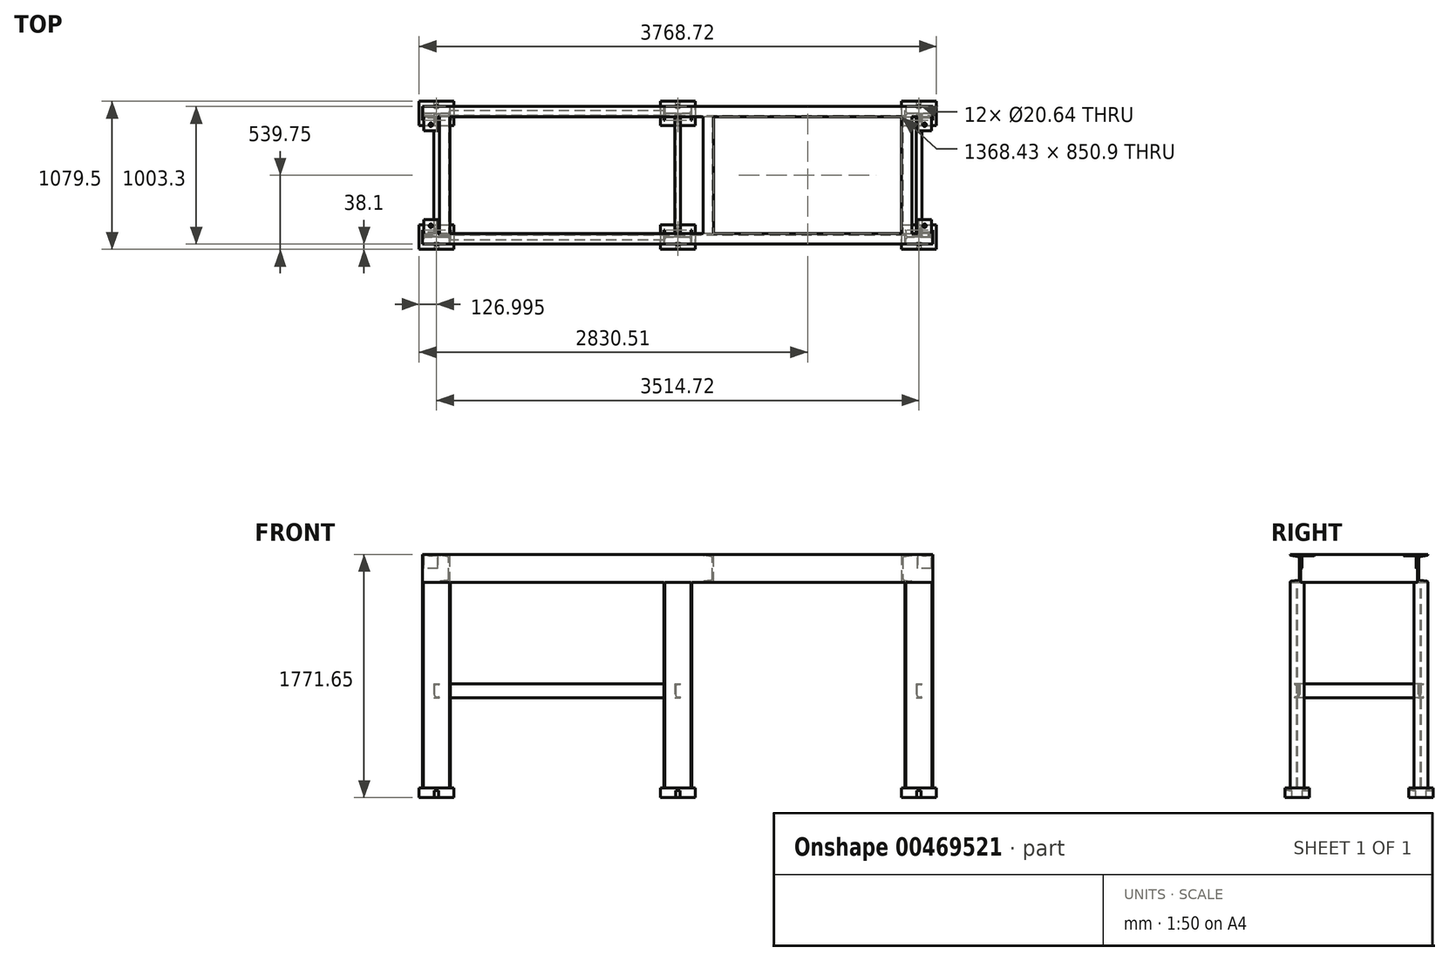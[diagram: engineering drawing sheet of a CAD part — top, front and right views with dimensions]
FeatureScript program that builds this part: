
annotation { "Feature Type Name" : "Feature", "Feature Type Description" : "" }
export const myFeature = defineFeature(function(context is Context, id is Id, definition is map)
    precondition{}
    {
        {
            var Q0;
            Q0=qCreatedBy(makeId("Right.planeOp"),FACE);
            var sketch = newSketch(context, id + "F0", { "sketchPlane" : qUnion([Q0])});
            skLineSegment(sketch, "E0", {"start": v(0, 0) * mm, "end": v(0, -101.6) * mm});
            skLineSegment(sketch, "E1", {"start": v(0, 0) * mm, "end": v(101.6, 0) * mm});
            skLineSegment(sketch, "E2", {"start": v(101.6, 0) * mm, "end": v(101.6, -4.76) * mm});
            skLineSegment(sketch, "E3", {"start": v(0, -101.6) * mm, "end": v(4.76, -101.6) * mm});
            skArc(sketch, "E4", {"start": v(4.76, -101.6) * mm, "mid": v(8.13, -100.2) * mm, "end": v(9.53, -96.84) * mm});
            skArc(sketch, "E5", {"start": v(96.84, -9.53) * mm, "mid": v(100.2, -8.13) * mm, "end": v(101.6, -4.76) * mm});
            skArc(sketch, "E6", {"start": v(19.05, -9.53) * mm, "mid": v(12.31, -12.31) * mm, "end": v(9.52, -19.05) * mm});
            skLineSegment(sketch, "E7", {"start": v(9.53, -96.84) * mm, "end": v(9.53, -19.05) * mm});
            skLineSegment(sketch, "E8", {"start": v(96.84, -9.53) * mm, "end": v(19.05, -9.53) * mm});
            skSolve(sketch);
        }
        {
            var Q0;
            Q0 = qSketchRegion(id + "F0", true);
            extrude(context, id + "F1", {"entities" : qUnion([Q0]), "endBound" : BoundingType.SYMMETRIC, "depth" : 101.6 * mm, "offsetDistance" : 25.4 * mm});
        }
        {
            var Q0;
            Q0=qCreatedBy(makeId("Right.planeOp"),FACE);
            var sketch = newSketch(context, id + "F2", { "sketchPlane" : qUnion([Q0])});
            skLineSegment(sketch, "E9", {"start": v(0, 0) * mm, "end": v(0, -203.2) * mm});
            skLineSegment(sketch, "E10", {"start": v(0, -203.2) * mm, "end": v(-76.2, -203.2) * mm});
            skLineSegment(sketch, "E11", {"start": v(0, 0) * mm, "end": v(-76.2, 0) * mm});
            skLineSegment(sketch, "E12", {"start": v(-9.53, -28.58) * mm, "end": v(-9.52, -174.62) * mm});
            skLineSegment(sketch, "E13", {"start": v(-19.35, -186.32) * mm, "end": v(-69.4, -195.1) * mm});
            skLineSegment(sketch, "E14", {"start": v(-19.35, -16.88) * mm, "end": v(-69.4, -8.1) * mm});
            skArc(sketch, "E15", {"start": v(-69.4, -195.1) * mm, "mid": v(-74.27, -197.91) * mm, "end": v(-76.2, -203.2) * mm});
            skArc(sketch, "E16", {"start": v(-76.2, 0) * mm, "mid": v(-74.27, -5.29) * mm, "end": v(-69.4, -8.1) * mm});
            skArc(sketch, "E17", {"start": v(-9.53, -28.58) * mm, "mid": v(-12.3, -20.94) * mm, "end": v(-19.35, -16.88) * mm});
            skArc(sketch, "E18", {"start": v(-19.35, -186.32) * mm, "mid": v(-12.3, -182.26) * mm, "end": v(-9.52, -174.62) * mm});
            skSolve(sketch);
        }
        {
            var Q0;
            Q0 = qSketchRegion(id + "F2", true);
            extrude(context, id + "F3", {"entities" : qUnion([Q0]), "operationType" : NewBodyOperationType.ADD, "oppositeDirection" : true, "depth" : 60.32 * mm, "offsetDistance" : 25.4 * mm, "hasSecondDirection" : true, "secondDirectionOppositeDirection" : false, "secondDirectionDepth" : 3657.6 * mm});
        }
        {
            var Q0;
            Q0=qCreatedBy(makeId("Right.planeOp"),FACE);
            cPlane(context, id + "F4", {"entities" : qUnion([Q0]), "cplaneType" : CPlaneType.OFFSET, "offset" : 3597.27 * mm, "width" : 152.4 * mm, "height" : 152.4 * mm});
        }
        {
            var Q0;
            Q0=qCreatedBy(id+"F4.planeOp",FACE);
            var sketch = newSketch(context, id + "F5", { "sketchPlane" : qUnion([Q0])});
            skLineSegment(sketch, "E19", {"start": v(0, 0) * mm, "end": v(0, -101.6) * mm});
            skLineSegment(sketch, "E20", {"start": v(0, 0) * mm, "end": v(101.6, 0) * mm});
            skLineSegment(sketch, "E21", {"start": v(101.6, 0) * mm, "end": v(101.6, -4.76) * mm});
            skLineSegment(sketch, "E22", {"start": v(0, -101.6) * mm, "end": v(4.76, -101.6) * mm});
            skArc(sketch, "E23", {"start": v(4.76, -101.6) * mm, "mid": v(8.13, -100.2) * mm, "end": v(9.53, -96.84) * mm});
            skArc(sketch, "E24", {"start": v(96.84, -9.53) * mm, "mid": v(100.2, -8.13) * mm, "end": v(101.6, -4.76) * mm});
            skArc(sketch, "E25", {"start": v(19.05, -9.53) * mm, "mid": v(12.31, -12.31) * mm, "end": v(9.52, -19.05) * mm});
            skLineSegment(sketch, "E26", {"start": v(9.53, -96.84) * mm, "end": v(9.53, -19.05) * mm});
            skLineSegment(sketch, "E27", {"start": v(96.84, -9.53) * mm, "end": v(19.05, -9.53) * mm});
            skSolve(sketch);
        }
        {
            var Q0;
            Q0 = qSketchRegion(id + "F5", true);
            extrude(context, id + "F6", {"entities" : qUnion([Q0]), "operationType" : NewBodyOperationType.ADD, "endBound" : BoundingType.SYMMETRIC, "depth" : 101.6 * mm, "offsetDistance" : 25.4 * mm});
        }
        {
            var Q0;
            Q0=makeQuery(id+"F1.opExtrude","SWEPT_FACE",FACE,{"disambiguationData":[OSD([sQuery(id+"F0.wireOp",EDGE,"E1")])]});
            var sketch = newSketch(context, id + "F7", { "sketchPlane" : qUnion([Q0])});
            skCircle(sketch, "E28", {"center": v(0, 57.15) * mm, "radius": 12.7 * mm});
            skCircle(sketch, "E29", {"center": v(3597.28, 57.15) * mm, "radius": 12.7 * mm});
            skSolve(sketch);
        }
        {
            var Q0;
            Q0 = qSketchRegion(id + "F7", true);
            extrude(context, id + "F8", {"entities" : qUnion([Q0]), "operationType" : NewBodyOperationType.REMOVE, "endBound" : BoundingType.UP_TO_NEXT, "oppositeDirection" : true, "depth" : 25.4 * mm, "offsetDistance" : 25.4 * mm});
        }
        {
            var Q0;
            Q0=qCreatedBy(makeId("Front.planeOp"),FACE);
            cPlane(context, id + "F9", {"entities" : qUnion([Q0]), "cplaneType" : CPlaneType.OFFSET, "offset" : 425.45 * mm, "oppositeDirection" : true, "width" : 152.4 * mm, "height" : 152.4 * mm});
        }
        {
            var Q0;
            Q0=makeQuery(id+"F1.opExtrude","SWEPT_BODY",BODY,{"disambiguationData":[OSD([sQuery(id+"F0.wireOp",EDGE,"E0"),sQuery(id+"F0.wireOp",EDGE,"E1"),sQuery(id+"F0.wireOp",EDGE,"E2"),sQuery(id+"F0.wireOp",EDGE,"E3"),sQuery(id+"F0.wireOp",EDGE,"E4"),sQuery(id+"F0.wireOp",EDGE,"E5"),sQuery(id+"F0.wireOp",EDGE,"E6"),sQuery(id+"F0.wireOp",EDGE,"E7"),sQuery(id+"F0.wireOp",EDGE,"E8")])]});
            var Q1;
            Q1=qCreatedBy(id+"F9.planeOp",FACE);
            mirror(context, id + "F10", {"entities" : qUnion([Q0]), "mirrorPlane" : qUnion([Q1])});
        }
        {
            var Q0;
            Q0=makeQuery(id+"F3.opExtrude","SWEPT_FACE",FACE,{"disambiguationData":[OSD([sQuery(id+"F2.wireOp",EDGE,"E9")])]});
            var sketch = newSketch(context, id + "F11", { "sketchPlane" : qUnion([Q0])});
            skLineSegment(sketch, "E30", {"start": v(-3429, 0) * mm, "end": v(-3429, -203.2) * mm});
            skLineSegment(sketch, "E31", {"start": v(-3429, -203.2) * mm, "end": v(-3505.2, -203.2) * mm});
            skLineSegment(sketch, "E32", {"start": v(-3429, 0) * mm, "end": v(-3505.2, 0) * mm});
            skLineSegment(sketch, "E33", {"start": v(-3438.53, -28.58) * mm, "end": v(-3438.53, -174.62) * mm});
            skLineSegment(sketch, "E34", {"start": v(-3448.35, -186.32) * mm, "end": v(-3498.4, -195.1) * mm});
            skLineSegment(sketch, "E35", {"start": v(-3448.35, -16.88) * mm, "end": v(-3498.4, -8.1) * mm});
            skArc(sketch, "E36", {"start": v(-3498.4, -195.1) * mm, "mid": v(-3503.27, -197.91) * mm, "end": v(-3505.2, -203.2) * mm});
            skArc(sketch, "E37", {"start": v(-3505.2, 0) * mm, "mid": v(-3503.27, -5.29) * mm, "end": v(-3498.4, -8.1) * mm});
            skArc(sketch, "E38", {"start": v(-3438.52, -28.58) * mm, "mid": v(-3441.3, -20.94) * mm, "end": v(-3448.35, -16.88) * mm});
            skArc(sketch, "E39", {"start": v(-3448.35, -186.32) * mm, "mid": v(-3441.3, -182.26) * mm, "end": v(-3438.53, -174.62) * mm});
            skLineSegment(sketch, "E40", {"start": v(-2060.57, -203.2) * mm, "end": v(-2060.57, 0) * mm});
            skLineSegment(sketch, "E41", {"start": v(-2060.57, 0) * mm, "end": v(-1984.38, 0) * mm});
            skLineSegment(sketch, "E42", {"start": v(-2060.57, -203.2) * mm, "end": v(-1984.38, -203.2) * mm});
            skLineSegment(sketch, "E43", {"start": v(-2051.05, -174.62) * mm, "end": v(-2051.05, -28.58) * mm});
            skLineSegment(sketch, "E44", {"start": v(-2041.23, -16.88) * mm, "end": v(-1991.18, -8.1) * mm});
            skLineSegment(sketch, "E45", {"start": v(-2041.23, -186.32) * mm, "end": v(-1991.18, -195.1) * mm});
            skArc(sketch, "E46", {"start": v(-1991.18, -8.1) * mm, "mid": v(-1986.3, -5.29) * mm, "end": v(-1984.38, 0) * mm});
            skArc(sketch, "E47", {"start": v(-1984.38, -203.2) * mm, "mid": v(-1986.3, -197.91) * mm, "end": v(-1991.18, -195.1) * mm});
            skArc(sketch, "E48", {"start": v(-2051.05, -174.62) * mm, "mid": v(-2048.27, -182.26) * mm, "end": v(-2041.23, -186.32) * mm});
            skArc(sketch, "E49", {"start": v(-2041.23, -16.88) * mm, "mid": v(-2048.27, -20.94) * mm, "end": v(-2051.05, -28.58) * mm});
            skLineSegment(sketch, "E50", {"start": v(-139.7, -203.2) * mm, "end": v(-139.7, 0) * mm});
            skLineSegment(sketch, "E51", {"start": v(-139.7, 0) * mm, "end": v(-63.5, 0) * mm});
            skLineSegment(sketch, "E52", {"start": v(-139.7, -203.2) * mm, "end": v(-63.5, -203.2) * mm});
            skLineSegment(sketch, "E53", {"start": v(-130.17, -174.62) * mm, "end": v(-130.17, -28.58) * mm});
            skLineSegment(sketch, "E54", {"start": v(-120.35, -16.88) * mm, "end": v(-70.3, -8.1) * mm});
            skLineSegment(sketch, "E55", {"start": v(-120.35, -186.32) * mm, "end": v(-70.3, -195.1) * mm});
            skArc(sketch, "E56", {"start": v(-70.3, -8.1) * mm, "mid": v(-65.43, -5.29) * mm, "end": v(-63.5, 0) * mm});
            skArc(sketch, "E57", {"start": v(-63.5, -203.2) * mm, "mid": v(-65.43, -197.91) * mm, "end": v(-70.3, -195.1) * mm});
            skArc(sketch, "E58", {"start": v(-130.18, -174.62) * mm, "mid": v(-127.4, -182.26) * mm, "end": v(-120.35, -186.32) * mm});
            skArc(sketch, "E59", {"start": v(-120.35, -16.88) * mm, "mid": v(-127.4, -20.94) * mm, "end": v(-130.18, -28.58) * mm});
            skSolve(sketch);
        }
        {
            var Q0;
            Q0 = qSketchRegion(id + "F11", true);
            extrude(context, id + "F12", {"entities" : qUnion([Q0]), "operationType" : NewBodyOperationType.ADD, "endBound" : BoundingType.UP_TO_NEXT, "depth" : 25.4 * mm, "offsetDistance" : 25.4 * mm});
        }
        {
            var Q0;
            {var subQ0=makeQuery(id+"F3.opExtrude","SWEPT_FACE",FACE,{"disambiguationData":[OSD([sQuery(id+"F2.wireOp",EDGE,"E10")])]});Q0=makeQuery(id+"F12.boolean.opBoolean","MERGE",FACE,{"derivedFrom":[subQ0,makeQuery(id+"F10.opPattern","COPY",FACE,{"derivedFrom":subQ0,"instanceName":"1"}),makeQuery(id+"F12.opExtrude","SWEPT_FACE",FACE,{"disambiguationData":[OSD([sQuery(id+"F11.wireOp",EDGE,"E31")])]}),makeQuery(id+"F12.opExtrude","SWEPT_FACE",FACE,{"disambiguationData":[OSD([sQuery(id+"F11.wireOp",EDGE,"E42")])]}),makeQuery(id+"F12.opExtrude","SWEPT_FACE",FACE,{"disambiguationData":[OSD([sQuery(id+"F11.wireOp",EDGE,"E52")])]})]});}
            var sketch = newSketch(context, id + "F13", { "sketchPlane" : qUnion([Q0])});
            skLineSegment(sketch, "E60", {"start": v(-60.33, -825.5) * mm, "end": v(-60.33, -927.1) * mm});
            skLineSegment(sketch, "E61", {"start": v(-60.33, -927.1) * mm, "end": v(-53.98, -927.1) * mm});
            skLineSegment(sketch, "E62", {"start": v(-60.33, -825.5) * mm, "end": v(-53.98, -825.5) * mm});
            skLineSegment(sketch, "E63", {"start": v(142.87, -825.5) * mm, "end": v(142.87, -927.1) * mm});
            skLineSegment(sketch, "E64", {"start": v(142.87, -927.1) * mm, "end": v(136.53, -927.1) * mm});
            skLineSegment(sketch, "E65", {"start": v(142.87, -825.5) * mm, "end": v(136.52, -825.5) * mm});
            skLineSegment(sketch, "E66", {"start": v(-53.98, -825.5) * mm, "end": v(-53.98, -860.42) * mm});
            skLineSegment(sketch, "E67", {"start": v(-53.98, -927.1) * mm, "end": v(-53.98, -892.17) * mm});
            skLineSegment(sketch, "E68", {"start": v(136.52, -927.1) * mm, "end": v(136.52, -892.17) * mm});
            skLineSegment(sketch, "E69", {"start": v(136.52, -825.5) * mm, "end": v(136.52, -860.43) * mm});
            skLineSegment(sketch, "E70", {"start": v(-41.28, -879.47) * mm, "end": v(123.83, -879.47) * mm});
            skLineSegment(sketch, "E71", {"start": v(123.83, -873.12) * mm, "end": v(-41.28, -873.12) * mm});
            skPoint(sketch, "E72.visualSharp", {"position": v(-53.98, -873.12) * mm});
            skArc(sketch, "E72.filletArc", {"start": v(-53.98, -860.42) * mm, "mid": v(-50.26, -869.4) * mm, "end": v(-41.28, -873.12) * mm});
            skPoint(sketch, "E73.visualSharp", {"position": v(-53.98, -879.47) * mm});
            skArc(sketch, "E73.filletArc", {"start": v(-41.28, -879.47) * mm, "mid": v(-50.26, -883.2) * mm, "end": v(-53.98, -892.17) * mm});
            skPoint(sketch, "E74.visualSharp", {"position": v(136.52, -873.12) * mm});
            skArc(sketch, "E74.filletArc", {"start": v(123.83, -873.13) * mm, "mid": v(132.8, -869.4) * mm, "end": v(136.53, -860.43) * mm});
            skPoint(sketch, "E75.visualSharp", {"position": v(136.52, -879.47) * mm});
            skArc(sketch, "E75.filletArc", {"start": v(136.53, -892.17) * mm, "mid": v(132.8, -883.2) * mm, "end": v(123.83, -879.47) * mm});
            skLineSegment(sketch, "E76.0.1.0", {"start": v(-60.33, 76.2) * mm, "end": v(-60.33, -25.4) * mm});
            skLineSegment(sketch, "E76.0.1.1", {"start": v(-60.33, 76.2) * mm, "end": v(-53.98, 76.2) * mm});
            skLineSegment(sketch, "E76.0.1.2", {"start": v(-53.98, 76.2) * mm, "end": v(-53.98, 41.28) * mm});
            skArc(sketch, "E76.0.1.3", {"start": v(-53.98, 41.28) * mm, "mid": v(-50.26, 32.3) * mm, "end": v(-41.28, 28.58) * mm});
            skArc(sketch, "E76.0.1.4", {"start": v(-41.28, 22.23) * mm, "mid": v(-50.26, 18.5) * mm, "end": v(-53.98, 9.53) * mm});
            skLineSegment(sketch, "E76.0.1.5", {"start": v(-53.98, -25.4) * mm, "end": v(-53.98, 9.53) * mm});
            skLineSegment(sketch, "E76.0.1.6", {"start": v(-60.33, -25.4) * mm, "end": v(-53.98, -25.4) * mm});
            skLineSegment(sketch, "E76.0.1.7", {"start": v(-41.28, 22.23) * mm, "end": v(123.83, 22.23) * mm});
            skLineSegment(sketch, "E76.0.1.8", {"start": v(123.83, 28.58) * mm, "end": v(-41.28, 28.58) * mm});
            skArc(sketch, "E76.0.1.9", {"start": v(123.83, 28.57) * mm, "mid": v(132.8, 32.3) * mm, "end": v(136.53, 41.27) * mm});
            skArc(sketch, "E76.0.1.10", {"start": v(136.53, 9.53) * mm, "mid": v(132.8, 18.5) * mm, "end": v(123.83, 22.23) * mm});
            skLineSegment(sketch, "E76.0.1.11", {"start": v(136.53, -25.4) * mm, "end": v(136.53, 9.53) * mm});
            skLineSegment(sketch, "E76.0.1.12", {"start": v(142.87, -25.4) * mm, "end": v(136.53, -25.4) * mm});
            skLineSegment(sketch, "E76.0.1.13", {"start": v(136.52, 76.2) * mm, "end": v(136.52, 41.27) * mm});
            skLineSegment(sketch, "E76.0.1.14", {"start": v(142.87, 76.2) * mm, "end": v(136.52, 76.2) * mm});
            skLineSegment(sketch, "E76.0.1.15", {"start": v(142.87, 76.2) * mm, "end": v(142.87, -25.4) * mm});
            skLineSegment(sketch, "E76.1.0.0", {"start": v(1697.04, -825.5) * mm, "end": v(1697.04, -927.1) * mm});
            skLineSegment(sketch, "E76.1.0.1", {"start": v(1697.04, -825.5) * mm, "end": v(1703.39, -825.5) * mm});
            skLineSegment(sketch, "E76.1.0.2", {"start": v(1703.39, -825.5) * mm, "end": v(1703.39, -860.42) * mm});
            skArc(sketch, "E76.1.0.3", {"start": v(1703.39, -860.42) * mm, "mid": v(1707.1, -869.4) * mm, "end": v(1716.09, -873.12) * mm});
            skArc(sketch, "E76.1.0.4", {"start": v(1716.09, -879.47) * mm, "mid": v(1707.1, -883.2) * mm, "end": v(1703.39, -892.17) * mm});
            skLineSegment(sketch, "E76.1.0.5", {"start": v(1703.39, -927.1) * mm, "end": v(1703.39, -892.17) * mm});
            skLineSegment(sketch, "E76.1.0.6", {"start": v(1697.04, -927.1) * mm, "end": v(1703.39, -927.1) * mm});
            skLineSegment(sketch, "E76.1.0.7", {"start": v(1716.09, -879.47) * mm, "end": v(1881.19, -879.47) * mm});
            skLineSegment(sketch, "E76.1.0.8", {"start": v(1881.19, -873.12) * mm, "end": v(1716.09, -873.12) * mm});
            skArc(sketch, "E76.1.0.9", {"start": v(1881.19, -873.13) * mm, "mid": v(1890.17, -869.4) * mm, "end": v(1893.89, -860.43) * mm});
            skArc(sketch, "E76.1.0.10", {"start": v(1893.89, -892.17) * mm, "mid": v(1890.17, -883.2) * mm, "end": v(1881.19, -879.47) * mm});
            skLineSegment(sketch, "E76.1.0.11", {"start": v(1893.89, -927.1) * mm, "end": v(1893.89, -892.17) * mm});
            skLineSegment(sketch, "E76.1.0.12", {"start": v(1900.24, -927.1) * mm, "end": v(1893.89, -927.1) * mm});
            skLineSegment(sketch, "E76.1.0.13", {"start": v(1893.89, -825.5) * mm, "end": v(1893.89, -860.43) * mm});
            skLineSegment(sketch, "E76.1.0.14", {"start": v(1900.24, -825.5) * mm, "end": v(1893.89, -825.5) * mm});
            skLineSegment(sketch, "E76.1.0.15", {"start": v(1900.24, -825.5) * mm, "end": v(1900.24, -927.1) * mm});
            skLineSegment(sketch, "E76.1.1.0", {"start": v(1697.04, 76.2) * mm, "end": v(1697.04, -25.4) * mm});
            skLineSegment(sketch, "E76.1.1.1", {"start": v(1697.04, 76.2) * mm, "end": v(1703.39, 76.2) * mm});
            skLineSegment(sketch, "E76.1.1.2", {"start": v(1703.39, 76.2) * mm, "end": v(1703.39, 41.28) * mm});
            skArc(sketch, "E76.1.1.3", {"start": v(1703.39, 41.28) * mm, "mid": v(1707.1, 32.3) * mm, "end": v(1716.09, 28.58) * mm});
            skArc(sketch, "E76.1.1.4", {"start": v(1716.09, 22.23) * mm, "mid": v(1707.1, 18.5) * mm, "end": v(1703.39, 9.53) * mm});
            skLineSegment(sketch, "E76.1.1.5", {"start": v(1703.39, -25.4) * mm, "end": v(1703.39, 9.53) * mm});
            skLineSegment(sketch, "E76.1.1.6", {"start": v(1697.04, -25.4) * mm, "end": v(1703.39, -25.4) * mm});
            skLineSegment(sketch, "E76.1.1.7", {"start": v(1716.09, 22.23) * mm, "end": v(1881.19, 22.23) * mm});
            skLineSegment(sketch, "E76.1.1.8", {"start": v(1881.19, 28.58) * mm, "end": v(1716.09, 28.58) * mm});
            skArc(sketch, "E76.1.1.9", {"start": v(1881.19, 28.57) * mm, "mid": v(1890.17, 32.3) * mm, "end": v(1893.89, 41.27) * mm});
            skArc(sketch, "E76.1.1.10", {"start": v(1893.89, 9.53) * mm, "mid": v(1890.17, 18.5) * mm, "end": v(1881.19, 22.23) * mm});
            skLineSegment(sketch, "E76.1.1.11", {"start": v(1893.89, -25.4) * mm, "end": v(1893.89, 9.53) * mm});
            skLineSegment(sketch, "E76.1.1.12", {"start": v(1900.24, -25.4) * mm, "end": v(1893.89, -25.4) * mm});
            skLineSegment(sketch, "E76.1.1.13", {"start": v(1893.89, 76.2) * mm, "end": v(1893.89, 41.27) * mm});
            skLineSegment(sketch, "E76.1.1.14", {"start": v(1900.24, 76.2) * mm, "end": v(1893.89, 76.2) * mm});
            skLineSegment(sketch, "E76.1.1.15", {"start": v(1900.24, 76.2) * mm, "end": v(1900.24, -25.4) * mm});
            skLineSegment(sketch, "E76.2.0.0", {"start": v(3454.4, -825.5) * mm, "end": v(3454.4, -927.1) * mm});
            skLineSegment(sketch, "E76.2.0.1", {"start": v(3454.4, -825.5) * mm, "end": v(3460.75, -825.5) * mm});
            skLineSegment(sketch, "E76.2.0.2", {"start": v(3460.75, -825.5) * mm, "end": v(3460.75, -860.42) * mm});
            skArc(sketch, "E76.2.0.3", {"start": v(3460.75, -860.42) * mm, "mid": v(3464.47, -869.4) * mm, "end": v(3473.45, -873.12) * mm});
            skArc(sketch, "E76.2.0.4", {"start": v(3473.45, -879.47) * mm, "mid": v(3464.47, -883.2) * mm, "end": v(3460.75, -892.17) * mm});
            skLineSegment(sketch, "E76.2.0.5", {"start": v(3460.75, -927.1) * mm, "end": v(3460.75, -892.17) * mm});
            skLineSegment(sketch, "E76.2.0.6", {"start": v(3454.4, -927.1) * mm, "end": v(3460.75, -927.1) * mm});
            skLineSegment(sketch, "E76.2.0.7", {"start": v(3473.45, -879.47) * mm, "end": v(3638.55, -879.47) * mm});
            skLineSegment(sketch, "E76.2.0.8", {"start": v(3638.55, -873.12) * mm, "end": v(3473.45, -873.12) * mm});
            skArc(sketch, "E76.2.0.9", {"start": v(3638.55, -873.13) * mm, "mid": v(3647.53, -869.4) * mm, "end": v(3651.25, -860.43) * mm});
            skArc(sketch, "E76.2.0.10", {"start": v(3651.25, -892.17) * mm, "mid": v(3647.53, -883.2) * mm, "end": v(3638.55, -879.47) * mm});
            skLineSegment(sketch, "E76.2.0.11", {"start": v(3651.25, -927.1) * mm, "end": v(3651.25, -892.17) * mm});
            skLineSegment(sketch, "E76.2.0.12", {"start": v(3657.6, -927.1) * mm, "end": v(3651.25, -927.1) * mm});
            skLineSegment(sketch, "E76.2.0.13", {"start": v(3651.25, -825.5) * mm, "end": v(3651.25, -860.43) * mm});
            skLineSegment(sketch, "E76.2.0.14", {"start": v(3657.6, -825.5) * mm, "end": v(3651.25, -825.5) * mm});
            skLineSegment(sketch, "E76.2.0.15", {"start": v(3657.6, -825.5) * mm, "end": v(3657.6, -927.1) * mm});
            skLineSegment(sketch, "E76.2.1.0", {"start": v(3454.4, 76.2) * mm, "end": v(3454.4, -25.4) * mm});
            skLineSegment(sketch, "E76.2.1.1", {"start": v(3454.4, 76.2) * mm, "end": v(3460.75, 76.2) * mm});
            skLineSegment(sketch, "E76.2.1.2", {"start": v(3460.75, 76.2) * mm, "end": v(3460.75, 41.28) * mm});
            skArc(sketch, "E76.2.1.3", {"start": v(3460.75, 41.28) * mm, "mid": v(3464.47, 32.3) * mm, "end": v(3473.45, 28.58) * mm});
            skArc(sketch, "E76.2.1.4", {"start": v(3473.45, 22.23) * mm, "mid": v(3464.47, 18.5) * mm, "end": v(3460.75, 9.53) * mm});
            skLineSegment(sketch, "E76.2.1.5", {"start": v(3460.75, -25.4) * mm, "end": v(3460.75, 9.53) * mm});
            skLineSegment(sketch, "E76.2.1.6", {"start": v(3454.4, -25.4) * mm, "end": v(3460.75, -25.4) * mm});
            skLineSegment(sketch, "E76.2.1.7", {"start": v(3473.45, 22.23) * mm, "end": v(3638.55, 22.23) * mm});
            skLineSegment(sketch, "E76.2.1.8", {"start": v(3638.55, 28.58) * mm, "end": v(3473.45, 28.58) * mm});
            skArc(sketch, "E76.2.1.9", {"start": v(3638.55, 28.57) * mm, "mid": v(3647.53, 32.3) * mm, "end": v(3651.25, 41.27) * mm});
            skArc(sketch, "E76.2.1.10", {"start": v(3651.25, 9.53) * mm, "mid": v(3647.53, 18.5) * mm, "end": v(3638.55, 22.23) * mm});
            skLineSegment(sketch, "E76.2.1.11", {"start": v(3651.25, -25.4) * mm, "end": v(3651.25, 9.53) * mm});
            skLineSegment(sketch, "E76.2.1.12", {"start": v(3657.6, -25.4) * mm, "end": v(3651.25, -25.4) * mm});
            skLineSegment(sketch, "E76.2.1.13", {"start": v(3651.25, 76.2) * mm, "end": v(3651.25, 41.27) * mm});
            skLineSegment(sketch, "E76.2.1.14", {"start": v(3657.6, 76.2) * mm, "end": v(3651.25, 76.2) * mm});
            skLineSegment(sketch, "E76.2.1.15", {"start": v(3657.6, 76.2) * mm, "end": v(3657.6, -25.4) * mm});
            skLineSegment(sketch, "E76.direction1", {"start": v(-60.33, -927.1) * mm, "end": v(1697.04, -927.1) * mm, "construction": true});
            skLineSegment(sketch, "E76.direction2", {"start": v(-60.33, -927.1) * mm, "end": v(-60.33, -25.4) * mm, "construction": true});
            skSolve(sketch);
        }
        {
            var Q0;
            Q0 = qSketchRegion(id + "F13", true);
            extrude(context, id + "F14", {"entities" : qUnion([Q0]), "operationType" : NewBodyOperationType.ADD, "depth" : 1498.6 * mm, "offsetDistance" : 25.4 * mm});
        }
        {
            var Q0;
            Q0=makeQuery(id+"F14.opExtrude","CAP_FACE",FACE,{"disambiguationData":[OSD([sQuery(id+"F13.wireOp",EDGE,"E76.0.1.0"),sQuery(id+"F13.wireOp",EDGE,"E76.0.1.1"),sQuery(id+"F13.wireOp",EDGE,"E76.0.1.2"),sQuery(id+"F13.wireOp",EDGE,"E76.0.1.3"),sQuery(id+"F13.wireOp",EDGE,"E76.0.1.4"),sQuery(id+"F13.wireOp",EDGE,"E76.0.1.5"),sQuery(id+"F13.wireOp",EDGE,"E76.0.1.6"),sQuery(id+"F13.wireOp",EDGE,"E76.0.1.7"),sQuery(id+"F13.wireOp",EDGE,"E76.0.1.8"),sQuery(id+"F13.wireOp",EDGE,"E76.0.1.9"),sQuery(id+"F13.wireOp",EDGE,"E76.0.1.10"),sQuery(id+"F13.wireOp",EDGE,"E76.0.1.11"),sQuery(id+"F13.wireOp",EDGE,"E76.0.1.12"),sQuery(id+"F13.wireOp",EDGE,"E76.0.1.13"),sQuery(id+"F13.wireOp",EDGE,"E76.0.1.14"),sQuery(id+"F13.wireOp",EDGE,"E76.0.1.15")])],"isStart":false});
            var sketch = newSketch(context, id + "F15", { "sketchPlane" : qUnion([Q0])});
            skLineSegment(sketch, "E77.bottom", {"start": v(-85.72, -63.5) * mm, "end": v(168.28, -63.5) * mm});
            skLineSegment(sketch, "E77.top", {"start": v(-85.72, 114.3) * mm, "end": v(168.28, 114.3) * mm});
            skLineSegment(sketch, "E77.left", {"start": v(-85.72, -63.5) * mm, "end": v(-85.72, 114.3) * mm});
            skLineSegment(sketch, "E77.right", {"start": v(168.28, -63.5) * mm, "end": v(168.28, 114.3) * mm});
            skPoint(sketch, "E77.middle", {"position": v(41.28, 25.4) * mm});
            skLineSegment(sketch, "E78", {"start": v(41.28, 28.58) * mm, "end": v(41.28, 22.23) * mm, "construction": true});
            skCircle(sketch, "E79", {"center": v(41.28, 76.2) * mm, "radius": 10.32 * mm});
            skCircle(sketch, "E80", {"center": v(41.28, -25.4) * mm, "radius": 10.32 * mm});
            skLineSegment(sketch, "E81", {"start": v(41.28, -25.4) * mm, "end": v(41.28, 76.2) * mm, "construction": true});
            skLineSegment(sketch, "E82.0.1.0", {"start": v(-85.72, -787.4) * mm, "end": v(168.28, -787.4) * mm});
            skLineSegment(sketch, "E82.0.1.1", {"start": v(-85.72, -965.2) * mm, "end": v(-85.72, -787.4) * mm});
            skLineSegment(sketch, "E82.0.1.2", {"start": v(-85.72, -965.2) * mm, "end": v(168.28, -965.2) * mm});
            skLineSegment(sketch, "E82.0.1.3", {"start": v(168.28, -965.2) * mm, "end": v(168.28, -787.4) * mm});
            skCircle(sketch, "E82.0.1.4", {"center": v(41.28, -927.1) * mm, "radius": 10.32 * mm});
            skCircle(sketch, "E82.0.1.5", {"center": v(41.28, -825.5) * mm, "radius": 10.32 * mm});
            skLineSegment(sketch, "E82.1.0.0", {"start": v(1671.64, 114.3) * mm, "end": v(1925.64, 114.3) * mm});
            skLineSegment(sketch, "E82.1.0.1", {"start": v(1671.64, -63.5) * mm, "end": v(1671.64, 114.3) * mm});
            skLineSegment(sketch, "E82.1.0.2", {"start": v(1671.64, -63.5) * mm, "end": v(1925.64, -63.5) * mm});
            skLineSegment(sketch, "E82.1.0.3", {"start": v(1925.64, -63.5) * mm, "end": v(1925.64, 114.3) * mm});
            skCircle(sketch, "E82.1.0.4", {"center": v(1798.64, -25.4) * mm, "radius": 10.32 * mm});
            skCircle(sketch, "E82.1.0.5", {"center": v(1798.64, 76.2) * mm, "radius": 10.32 * mm});
            skLineSegment(sketch, "E82.1.1.0", {"start": v(1671.64, -787.4) * mm, "end": v(1925.64, -787.4) * mm});
            skLineSegment(sketch, "E82.1.1.1", {"start": v(1671.64, -965.2) * mm, "end": v(1671.64, -787.4) * mm});
            skLineSegment(sketch, "E82.1.1.2", {"start": v(1671.64, -965.2) * mm, "end": v(1925.64, -965.2) * mm});
            skLineSegment(sketch, "E82.1.1.3", {"start": v(1925.64, -965.2) * mm, "end": v(1925.64, -787.4) * mm});
            skCircle(sketch, "E82.1.1.4", {"center": v(1798.64, -927.1) * mm, "radius": 10.32 * mm});
            skCircle(sketch, "E82.1.1.5", {"center": v(1798.64, -825.5) * mm, "radius": 10.32 * mm});
            skLineSegment(sketch, "E82.2.0.0", {"start": v(3429, 114.3) * mm, "end": v(3683, 114.3) * mm});
            skLineSegment(sketch, "E82.2.0.1", {"start": v(3429, -63.5) * mm, "end": v(3429, 114.3) * mm});
            skLineSegment(sketch, "E82.2.0.2", {"start": v(3429, -63.5) * mm, "end": v(3683, -63.5) * mm});
            skLineSegment(sketch, "E82.2.0.3", {"start": v(3683, -63.5) * mm, "end": v(3683, 114.3) * mm});
            skCircle(sketch, "E82.2.0.4", {"center": v(3556, -25.4) * mm, "radius": 10.32 * mm});
            skCircle(sketch, "E82.2.0.5", {"center": v(3556, 76.2) * mm, "radius": 10.32 * mm});
            skLineSegment(sketch, "E82.2.1.0", {"start": v(3429, -787.4) * mm, "end": v(3683, -787.4) * mm});
            skLineSegment(sketch, "E82.2.1.1", {"start": v(3429, -965.2) * mm, "end": v(3429, -787.4) * mm});
            skLineSegment(sketch, "E82.2.1.2", {"start": v(3429, -965.2) * mm, "end": v(3683, -965.2) * mm});
            skLineSegment(sketch, "E82.2.1.3", {"start": v(3683, -965.2) * mm, "end": v(3683, -787.4) * mm});
            skCircle(sketch, "E82.2.1.4", {"center": v(3556, -927.1) * mm, "radius": 10.32 * mm});
            skCircle(sketch, "E82.2.1.5", {"center": v(3556, -825.5) * mm, "radius": 10.32 * mm});
            skLineSegment(sketch, "E82.direction1", {"start": v(-85.72, 114.3) * mm, "end": v(1671.64, 114.3) * mm, "construction": true});
            skLineSegment(sketch, "E82.direction2", {"start": v(-85.72, 114.3) * mm, "end": v(-85.72, -787.4) * mm, "construction": true});
            skSolve(sketch);
        }
        {
            var Q0;
            Q0=makeQuery(id+"F15.imprint","IMPRINT",FACE,{"disambiguationData":[TD([[makeQuery(id+"F15.imprint","IMPRINT",EDGE,{"derivedFrom":sQuery(id+"F15.wireOp",EDGE,"E77.bottom")}),1.0]])]});
            var Q1;
            Q1=makeQuery(id+"F15.imprint","IMPRINT",FACE,{"disambiguationData":[TD([[makeQuery(id+"F15.imprint","IMPRINT",EDGE,{"derivedFrom":makeQuery(id+"F14.opExtrude","CAP_EDGE",EDGE,{"disambiguationData":[OSD([sQuery(id+"F13.wireOp",EDGE,"E76.0.1.0")])],"isStart":false})}),1.0]])]});
            var Q2;
            Q2=makeQuery(id+"F15.imprint","IMPRINT",FACE,{"disambiguationData":[TD([[makeQuery(id+"F15.imprint","IMPRINT",EDGE,{"derivedFrom":sQuery(id+"F15.wireOp",EDGE,"E82.1.0.0")}),-1.0]])]});
            var Q3;
            Q3=makeQuery(id+"F15.imprint","IMPRINT",FACE,{"disambiguationData":[TD([[makeQuery(id+"F15.imprint","IMPRINT",EDGE,{"derivedFrom":sQuery(id+"F15.wireOp",EDGE,"E82.2.0.0")}),-1.0]])]});
            var Q4;
            Q4=makeQuery(id+"F15.imprint","IMPRINT",FACE,{"disambiguationData":[TD([[makeQuery(id+"F15.imprint","IMPRINT",EDGE,{"derivedFrom":sQuery(id+"F15.wireOp",EDGE,"E82.2.1.0")}),-1.0]])]});
            var Q5;
            Q5=makeQuery(id+"F15.imprint","IMPRINT",FACE,{"disambiguationData":[TD([[makeQuery(id+"F15.imprint","IMPRINT",EDGE,{"derivedFrom":sQuery(id+"F15.wireOp",EDGE,"E82.1.1.0")}),-1.0]])]});
            var Q6;
            Q6=makeQuery(id+"F15.imprint","IMPRINT",FACE,{"disambiguationData":[TD([[makeQuery(id+"F15.imprint","IMPRINT",EDGE,{"derivedFrom":sQuery(id+"F15.wireOp",EDGE,"E82.0.1.0")}),-1.0]])]});
            extrude(context, id + "F16", {"entities" : qUnion([Q0, Q1, Q2, Q3, Q4, Q5, Q6]), "operationType" : NewBodyOperationType.ADD, "surfaceOperationType" : NewSurfaceOperationType.ADD, "depth" : 19.05 * mm, "offsetDistance" : 25.4 * mm});
        }
        {
            var Q0;
            Q0=makeQuery(id+"F16.opExtrude","CAP_FACE",FACE,{"disambiguationData":[OSD([sQuery(id+"F15.wireOp",EDGE,"E77.bottom"),sQuery(id+"F15.wireOp",EDGE,"E77.top"),sQuery(id+"F15.wireOp",EDGE,"E77.left"),sQuery(id+"F15.wireOp",EDGE,"E77.right"),sQuery(id+"F15.wireOp",EDGE,"E79"),sQuery(id+"F15.wireOp",EDGE,"E80")])],"isStart":false});
            var sketch = newSketch(context, id + "F17", { "sketchPlane" : qUnion([Q0])});
            skLineSegment(sketch, "E83.bottom", {"start": v(-85.72, 114.3) * mm, "end": v(168.28, 114.3) * mm});
            skLineSegment(sketch, "E83.top", {"start": v(-85.72, -63.5) * mm, "end": v(168.28, -63.5) * mm});
            skLineSegment(sketch, "E83.left", {"start": v(-85.72, 114.3) * mm, "end": v(-85.72, -63.5) * mm});
            skLineSegment(sketch, "E83.right", {"start": v(168.28, 114.3) * mm, "end": v(168.28, -63.5) * mm});
            skLineSegment(sketch, "E84.bottom", {"start": v(25.4, -12.7) * mm, "end": v(57.15, -12.7) * mm});
            skLineSegment(sketch, "E84.top", {"start": v(25.4, -63.5) * mm, "end": v(57.15, -63.5) * mm});
            skLineSegment(sketch, "E84.left", {"start": v(25.4, -12.7) * mm, "end": v(25.4, -63.5) * mm});
            skLineSegment(sketch, "E84.right", {"start": v(57.15, -12.7) * mm, "end": v(57.15, -63.5) * mm});
            skLineSegment(sketch, "E85.bottom", {"start": v(25.4, 63.5) * mm, "end": v(57.15, 63.5) * mm});
            skLineSegment(sketch, "E85.top", {"start": v(25.4, 114.3) * mm, "end": v(57.15, 114.3) * mm});
            skLineSegment(sketch, "E85.left", {"start": v(25.4, 63.5) * mm, "end": v(25.4, 114.3) * mm});
            skLineSegment(sketch, "E85.right", {"start": v(57.15, 63.5) * mm, "end": v(57.15, 114.3) * mm});
            skLineSegment(sketch, "E86.0.1.0", {"start": v(-85.72, -787.4) * mm, "end": v(168.28, -787.4) * mm});
            skLineSegment(sketch, "E86.0.1.1", {"start": v(-85.72, -787.4) * mm, "end": v(-85.72, -965.2) * mm});
            skLineSegment(sketch, "E86.0.1.2", {"start": v(168.28, -787.4) * mm, "end": v(168.28, -965.2) * mm});
            skLineSegment(sketch, "E86.0.1.3", {"start": v(25.4, -787.4) * mm, "end": v(57.15, -787.4) * mm});
            skLineSegment(sketch, "E86.0.1.4", {"start": v(25.4, -838.2) * mm, "end": v(25.4, -787.4) * mm});
            skLineSegment(sketch, "E86.0.1.5", {"start": v(57.15, -838.2) * mm, "end": v(57.15, -787.4) * mm});
            skLineSegment(sketch, "E86.0.1.6", {"start": v(25.4, -838.2) * mm, "end": v(57.15, -838.2) * mm});
            skLineSegment(sketch, "E86.0.1.7", {"start": v(25.4, -914.4) * mm, "end": v(57.15, -914.4) * mm});
            skLineSegment(sketch, "E86.0.1.8", {"start": v(25.4, -914.4) * mm, "end": v(25.4, -965.2) * mm});
            skLineSegment(sketch, "E86.0.1.9", {"start": v(57.15, -914.4) * mm, "end": v(57.15, -965.2) * mm});
            skLineSegment(sketch, "E86.0.1.10", {"start": v(25.4, -965.2) * mm, "end": v(57.15, -965.2) * mm});
            skLineSegment(sketch, "E86.0.1.11", {"start": v(-85.72, -965.2) * mm, "end": v(168.28, -965.2) * mm});
            skLineSegment(sketch, "E86.1.0.0", {"start": v(1671.64, 114.3) * mm, "end": v(1925.64, 114.3) * mm});
            skLineSegment(sketch, "E86.1.0.1", {"start": v(1671.64, 114.3) * mm, "end": v(1671.64, -63.5) * mm});
            skLineSegment(sketch, "E86.1.0.2", {"start": v(1925.64, 114.3) * mm, "end": v(1925.64, -63.5) * mm});
            skLineSegment(sketch, "E86.1.0.3", {"start": v(1782.76, 114.3) * mm, "end": v(1814.51, 114.3) * mm});
            skLineSegment(sketch, "E86.1.0.4", {"start": v(1782.76, 63.5) * mm, "end": v(1782.76, 114.3) * mm});
            skLineSegment(sketch, "E86.1.0.5", {"start": v(1814.51, 63.5) * mm, "end": v(1814.51, 114.3) * mm});
            skLineSegment(sketch, "E86.1.0.6", {"start": v(1782.76, 63.5) * mm, "end": v(1814.51, 63.5) * mm});
            skLineSegment(sketch, "E86.1.0.7", {"start": v(1782.76, -12.7) * mm, "end": v(1814.51, -12.7) * mm});
            skLineSegment(sketch, "E86.1.0.8", {"start": v(1782.76, -12.7) * mm, "end": v(1782.76, -63.5) * mm});
            skLineSegment(sketch, "E86.1.0.9", {"start": v(1814.51, -12.7) * mm, "end": v(1814.51, -63.5) * mm});
            skLineSegment(sketch, "E86.1.0.10", {"start": v(1782.76, -63.5) * mm, "end": v(1814.51, -63.5) * mm});
            skLineSegment(sketch, "E86.1.0.11", {"start": v(1671.64, -63.5) * mm, "end": v(1925.64, -63.5) * mm});
            skLineSegment(sketch, "E86.1.1.0", {"start": v(1671.64, -787.4) * mm, "end": v(1925.64, -787.4) * mm});
            skLineSegment(sketch, "E86.1.1.1", {"start": v(1671.64, -787.4) * mm, "end": v(1671.64, -965.2) * mm});
            skLineSegment(sketch, "E86.1.1.2", {"start": v(1925.64, -787.4) * mm, "end": v(1925.64, -965.2) * mm});
            skLineSegment(sketch, "E86.1.1.3", {"start": v(1782.76, -787.4) * mm, "end": v(1814.51, -787.4) * mm});
            skLineSegment(sketch, "E86.1.1.4", {"start": v(1782.76, -838.2) * mm, "end": v(1782.76, -787.4) * mm});
            skLineSegment(sketch, "E86.1.1.5", {"start": v(1814.51, -838.2) * mm, "end": v(1814.51, -787.4) * mm});
            skLineSegment(sketch, "E86.1.1.6", {"start": v(1782.76, -838.2) * mm, "end": v(1814.51, -838.2) * mm});
            skLineSegment(sketch, "E86.1.1.7", {"start": v(1782.76, -914.4) * mm, "end": v(1814.51, -914.4) * mm});
            skLineSegment(sketch, "E86.1.1.8", {"start": v(1782.76, -914.4) * mm, "end": v(1782.76, -965.2) * mm});
            skLineSegment(sketch, "E86.1.1.9", {"start": v(1814.51, -914.4) * mm, "end": v(1814.51, -965.2) * mm});
            skLineSegment(sketch, "E86.1.1.10", {"start": v(1782.76, -965.2) * mm, "end": v(1814.51, -965.2) * mm});
            skLineSegment(sketch, "E86.1.1.11", {"start": v(1671.64, -965.2) * mm, "end": v(1925.64, -965.2) * mm});
            skLineSegment(sketch, "E86.2.0.0", {"start": v(3429, 114.3) * mm, "end": v(3683, 114.3) * mm});
            skLineSegment(sketch, "E86.2.0.1", {"start": v(3429, 114.3) * mm, "end": v(3429, -63.5) * mm});
            skLineSegment(sketch, "E86.2.0.2", {"start": v(3683, 114.3) * mm, "end": v(3683, -63.5) * mm});
            skLineSegment(sketch, "E86.2.0.3", {"start": v(3540.13, 114.3) * mm, "end": v(3571.88, 114.3) * mm});
            skLineSegment(sketch, "E86.2.0.4", {"start": v(3540.13, 63.5) * mm, "end": v(3540.13, 114.3) * mm});
            skLineSegment(sketch, "E86.2.0.5", {"start": v(3571.88, 63.5) * mm, "end": v(3571.88, 114.3) * mm});
            skLineSegment(sketch, "E86.2.0.6", {"start": v(3540.12, 63.5) * mm, "end": v(3571.88, 63.5) * mm});
            skLineSegment(sketch, "E86.2.0.7", {"start": v(3540.13, -12.7) * mm, "end": v(3571.88, -12.7) * mm});
            skLineSegment(sketch, "E86.2.0.8", {"start": v(3540.13, -12.7) * mm, "end": v(3540.13, -63.5) * mm});
            skLineSegment(sketch, "E86.2.0.9", {"start": v(3571.88, -12.7) * mm, "end": v(3571.88, -63.5) * mm});
            skLineSegment(sketch, "E86.2.0.10", {"start": v(3540.13, -63.5) * mm, "end": v(3571.88, -63.5) * mm});
            skLineSegment(sketch, "E86.2.0.11", {"start": v(3429, -63.5) * mm, "end": v(3683, -63.5) * mm});
            skLineSegment(sketch, "E86.2.1.0", {"start": v(3429, -787.4) * mm, "end": v(3683, -787.4) * mm});
            skLineSegment(sketch, "E86.2.1.1", {"start": v(3429, -787.4) * mm, "end": v(3429, -965.2) * mm});
            skLineSegment(sketch, "E86.2.1.2", {"start": v(3683, -787.4) * mm, "end": v(3683, -965.2) * mm});
            skLineSegment(sketch, "E86.2.1.3", {"start": v(3540.13, -787.4) * mm, "end": v(3571.88, -787.4) * mm});
            skLineSegment(sketch, "E86.2.1.4", {"start": v(3540.13, -838.2) * mm, "end": v(3540.13, -787.4) * mm});
            skLineSegment(sketch, "E86.2.1.5", {"start": v(3571.88, -838.2) * mm, "end": v(3571.88, -787.4) * mm});
            skLineSegment(sketch, "E86.2.1.6", {"start": v(3540.12, -838.2) * mm, "end": v(3571.88, -838.2) * mm});
            skLineSegment(sketch, "E86.2.1.7", {"start": v(3540.13, -914.4) * mm, "end": v(3571.88, -914.4) * mm});
            skLineSegment(sketch, "E86.2.1.8", {"start": v(3540.13, -914.4) * mm, "end": v(3540.13, -965.2) * mm});
            skLineSegment(sketch, "E86.2.1.9", {"start": v(3571.88, -914.4) * mm, "end": v(3571.88, -965.2) * mm});
            skLineSegment(sketch, "E86.2.1.10", {"start": v(3540.13, -965.2) * mm, "end": v(3571.88, -965.2) * mm});
            skLineSegment(sketch, "E86.2.1.11", {"start": v(3429, -965.2) * mm, "end": v(3683, -965.2) * mm});
            skLineSegment(sketch, "E86.direction1", {"start": v(-85.72, 114.3) * mm, "end": v(1671.64, 114.3) * mm, "construction": true});
            skLineSegment(sketch, "E86.direction2", {"start": v(-85.72, 114.3) * mm, "end": v(-85.72, -787.4) * mm, "construction": true});
            skSolve(sketch);
        }
        {
            var Q0;
            {var subQ3=sQuery(id+"F17.wireOp",EDGE,"E83.left");Q0=makeQuery(id+"F17.imprint","IMPRINT",FACE,{"disambiguationData":[TD([[makeQuery(id+"F17.imprint","IMPRINT",EDGE,{"derivedFrom":subQ3}),-1.0]])]});}
            var Q1;
            {var subQ4=sQuery(id+"F17.wireOp",EDGE,"E86.1.0.1");Q1=makeQuery(id+"F17.imprint","IMPRINT",FACE,{"disambiguationData":[TD([[makeQuery(id+"F17.imprint","IMPRINT",EDGE,{"derivedFrom":subQ4}),1.0]])]});}
            var Q2;
            {var subQ4=sQuery(id+"F17.wireOp",EDGE,"E86.2.0.1");Q2=makeQuery(id+"F17.imprint","IMPRINT",FACE,{"disambiguationData":[TD([[makeQuery(id+"F17.imprint","IMPRINT",EDGE,{"derivedFrom":subQ4}),1.0]])]});}
            var Q3;
            {var subQ4=sQuery(id+"F17.wireOp",EDGE,"E86.2.1.1");Q3=makeQuery(id+"F17.imprint","IMPRINT",FACE,{"disambiguationData":[TD([[makeQuery(id+"F17.imprint","IMPRINT",EDGE,{"derivedFrom":subQ4}),1.0]])]});}
            var Q4;
            {var subQ4=sQuery(id+"F17.wireOp",EDGE,"E86.1.1.1");Q4=makeQuery(id+"F17.imprint","IMPRINT",FACE,{"disambiguationData":[TD([[makeQuery(id+"F17.imprint","IMPRINT",EDGE,{"derivedFrom":subQ4}),1.0]])]});}
            var Q5;
            {var subQ4=sQuery(id+"F17.wireOp",EDGE,"E86.0.1.1");Q5=makeQuery(id+"F17.imprint","IMPRINT",FACE,{"disambiguationData":[TD([[makeQuery(id+"F17.imprint","IMPRINT",EDGE,{"derivedFrom":subQ4}),1.0]])]});}
            extrude(context, id + "F18", {"entities" : qUnion([Q0, Q1, Q2, Q3, Q4, Q5]), "operationType" : NewBodyOperationType.ADD, "depth" : 50.8 * mm, "offsetDistance" : 25.4 * mm});
        }
        {
            var Q0;
            Q0=makeQuery(id+"F14.opExtrude","SWEPT_FACE",FACE,{"disambiguationData":[OSD([sQuery(id+"F13.wireOp",EDGE,"E76.0.1.7")])]});
            var sketch = newSketch(context, id + "F19", { "sketchPlane" : qUnion([Q0])});
            skLineSegment(sketch, "E87", {"start": v(-20.64, -942.98) * mm, "end": v(-20.64, -1044.58) * mm});
            skLineSegment(sketch, "E88", {"start": v(-20.64, -1044.58) * mm, "end": v(-61.91, -1044.58) * mm});
            skLineSegment(sketch, "E89", {"start": v(-20.64, -942.98) * mm, "end": v(-61.91, -942.98) * mm});
            skLineSegment(sketch, "E90", {"start": v(-25.3, -962.03) * mm, "end": v(-25.3, -1025.52) * mm});
            skLineSegment(sketch, "E91", {"start": v(-57.29, -948.5) * mm, "end": v(-32.93, -952.9) * mm});
            skLineSegment(sketch, "E92", {"start": v(-32.93, -1034.65) * mm, "end": v(-57.29, -1039.04) * mm});
            skArc(sketch, "E93", {"start": v(-32.93, -1034.65) * mm, "mid": v(-27.46, -1031.47) * mm, "end": v(-25.3, -1025.52) * mm});
            skArc(sketch, "E94", {"start": v(-25.3, -962.03) * mm, "mid": v(-27.46, -956.08) * mm, "end": v(-32.93, -952.9) * mm});
            skArc(sketch, "E95", {"start": v(-57.29, -1039.04) * mm, "mid": v(-60.6, -1040.97) * mm, "end": v(-61.91, -1044.58) * mm});
            skArc(sketch, "E96", {"start": v(-61.91, -942.98) * mm, "mid": v(-60.6, -946.58) * mm, "end": v(-57.29, -948.5) * mm});
            skLineSegment(sketch, "E97", {"start": v(-61.91, -1044.58) * mm, "end": v(-142.88, -1044.58) * mm, "construction": true});
            skLineSegment(sketch, "E98", {"start": v(-20.64, -1044.58) * mm, "end": v(60.32, -1044.58) * mm, "construction": true});
            skLineSegment(sketch, "E99.1.0.0", {"start": v(-1778, -942.98) * mm, "end": v(-1819.28, -942.98) * mm});
            skArc(sketch, "E99.1.0.1", {"start": v(-1819.28, -942.98) * mm, "mid": v(-1817.97, -946.58) * mm, "end": v(-1814.65, -948.5) * mm});
            skLineSegment(sketch, "E99.1.0.2", {"start": v(-1814.65, -948.5) * mm, "end": v(-1790.3, -952.9) * mm});
            skArc(sketch, "E99.1.0.3", {"start": v(-1782.66, -962.03) * mm, "mid": v(-1784.82, -956.08) * mm, "end": v(-1790.3, -952.9) * mm});
            skLineSegment(sketch, "E99.1.0.4", {"start": v(-1778, -942.98) * mm, "end": v(-1778, -1044.58) * mm});
            skLineSegment(sketch, "E99.1.0.5", {"start": v(-1782.66, -962.03) * mm, "end": v(-1782.66, -1025.52) * mm});
            skArc(sketch, "E99.1.0.6", {"start": v(-1790.3, -1034.65) * mm, "mid": v(-1784.82, -1031.47) * mm, "end": v(-1782.66, -1025.52) * mm});
            skLineSegment(sketch, "E99.1.0.7", {"start": v(-1790.3, -1034.65) * mm, "end": v(-1814.65, -1039.04) * mm});
            skArc(sketch, "E99.1.0.8", {"start": v(-1814.65, -1039.04) * mm, "mid": v(-1817.97, -1040.97) * mm, "end": v(-1819.28, -1044.58) * mm});
            skLineSegment(sketch, "E99.1.0.9", {"start": v(-1778, -1044.58) * mm, "end": v(-1819.28, -1044.58) * mm});
            skLineSegment(sketch, "E99.2.0.0", {"start": v(-3535.36, -942.98) * mm, "end": v(-3576.64, -942.98) * mm});
            skArc(sketch, "E99.2.0.1", {"start": v(-3576.64, -942.98) * mm, "mid": v(-3575.33, -946.58) * mm, "end": v(-3572.01, -948.5) * mm});
            skLineSegment(sketch, "E99.2.0.2", {"start": v(-3572.01, -948.5) * mm, "end": v(-3547.66, -952.9) * mm});
            skArc(sketch, "E99.2.0.3", {"start": v(-3540.03, -962.03) * mm, "mid": v(-3542.19, -956.08) * mm, "end": v(-3547.66, -952.9) * mm});
            skLineSegment(sketch, "E99.2.0.4", {"start": v(-3535.36, -942.98) * mm, "end": v(-3535.36, -1044.58) * mm});
            skLineSegment(sketch, "E99.2.0.5", {"start": v(-3540.03, -962.03) * mm, "end": v(-3540.03, -1025.52) * mm});
            skArc(sketch, "E99.2.0.6", {"start": v(-3547.66, -1034.65) * mm, "mid": v(-3542.19, -1031.47) * mm, "end": v(-3540.03, -1025.52) * mm});
            skLineSegment(sketch, "E99.2.0.7", {"start": v(-3547.66, -1034.65) * mm, "end": v(-3572.01, -1039.04) * mm});
            skArc(sketch, "E99.2.0.8", {"start": v(-3572.01, -1039.04) * mm, "mid": v(-3575.33, -1040.97) * mm, "end": v(-3576.64, -1044.58) * mm});
            skLineSegment(sketch, "E99.2.0.9", {"start": v(-3535.36, -1044.58) * mm, "end": v(-3576.64, -1044.58) * mm});
            skLineSegment(sketch, "E99.direction1", {"start": v(-61.91, -942.98) * mm, "end": v(-1819.28, -942.98) * mm, "construction": true});
            skSolve(sketch);
        }
        {
            var Q0;
            Q0 = qSketchRegion(id + "F19", true);
            extrude(context, id + "F20", {"entities" : qUnion([Q0]), "operationType" : NewBodyOperationType.ADD, "endBound" : BoundingType.UP_TO_NEXT, "depth" : 25.4 * mm, "offsetDistance" : 25.4 * mm});
        }
        {
            var Q0;
            Q0=makeQuery(id+"F14.opExtrude","SWEPT_FACE",FACE,{"disambiguationData":[OSD([sQuery(id+"F13.wireOp",EDGE,"E76.0.1.15")])]});
            var sketch = newSketch(context, id + "F21", { "sketchPlane" : qUnion([Q0])});
            skLineSegment(sketch, "E100", {"start": v(-4.76, -942.98) * mm, "end": v(-4.76, -1044.58) * mm});
            skLineSegment(sketch, "E101", {"start": v(-4.76, -1044.58) * mm, "end": v(-46.04, -1044.58) * mm});
            skLineSegment(sketch, "E102", {"start": v(-4.76, -942.98) * mm, "end": v(-46.04, -942.98) * mm});
            skLineSegment(sketch, "E103", {"start": v(-9.43, -962.03) * mm, "end": v(-9.43, -1025.52) * mm});
            skLineSegment(sketch, "E104", {"start": v(-41.41, -948.5) * mm, "end": v(-17.06, -952.9) * mm});
            skLineSegment(sketch, "E105", {"start": v(-17.06, -1034.65) * mm, "end": v(-41.41, -1039.04) * mm});
            skArc(sketch, "E106", {"start": v(-17.06, -1034.65) * mm, "mid": v(-11.59, -1031.47) * mm, "end": v(-9.43, -1025.52) * mm});
            skArc(sketch, "E107", {"start": v(-9.43, -962.03) * mm, "mid": v(-11.59, -956.08) * mm, "end": v(-17.06, -952.9) * mm});
            skArc(sketch, "E108", {"start": v(-41.41, -1039.04) * mm, "mid": v(-44.73, -1040.97) * mm, "end": v(-46.04, -1044.58) * mm});
            skArc(sketch, "E109", {"start": v(-46.04, -942.98) * mm, "mid": v(-44.73, -946.58) * mm, "end": v(-41.41, -948.5) * mm});
            skLineSegment(sketch, "E110", {"start": v(-46.04, -1044.58) * mm, "end": v(-76.2, -1044.58) * mm, "construction": true});
            skLineSegment(sketch, "E111", {"start": v(-4.76, -1044.58) * mm, "end": v(25.4, -1044.58) * mm, "construction": true});
            skLineSegment(sketch, "E112", {"start": v(425.45, -942.98) * mm, "end": v(425.45, -1044.58) * mm, "construction": true});
            skArc(sketch, "E113.MirrorCS", {"start": v(892.31, -1039.04) * mm, "mid": v(895.63, -1040.97) * mm, "end": v(896.94, -1044.58) * mm});
            skLineSegment(sketch, "E114.MirrorCS", {"start": v(855.66, -1044.58) * mm, "end": v(896.94, -1044.58) * mm});
            skLineSegment(sketch, "E115.MirrorCS", {"start": v(867.96, -1034.65) * mm, "end": v(892.31, -1039.04) * mm});
            skArc(sketch, "E116.MirrorCS", {"start": v(867.96, -1034.65) * mm, "mid": v(862.49, -1031.47) * mm, "end": v(860.33, -1025.52) * mm});
            skLineSegment(sketch, "E117.MirrorCS", {"start": v(855.66, -942.98) * mm, "end": v(855.66, -1044.58) * mm});
            skLineSegment(sketch, "E118.MirrorCS", {"start": v(860.33, -962.03) * mm, "end": v(860.33, -1025.52) * mm});
            skArc(sketch, "E119.MirrorCS", {"start": v(896.94, -942.98) * mm, "mid": v(895.63, -946.58) * mm, "end": v(892.31, -948.5) * mm});
            skLineSegment(sketch, "E120.MirrorCS", {"start": v(892.31, -948.5) * mm, "end": v(867.96, -952.9) * mm});
            skArc(sketch, "E121.MirrorCS", {"start": v(860.33, -962.03) * mm, "mid": v(862.49, -956.08) * mm, "end": v(867.96, -952.9) * mm});
            skLineSegment(sketch, "E122.MirrorCS", {"start": v(855.66, -942.98) * mm, "end": v(896.94, -942.98) * mm});
            skSolve(sketch);
        }
        {
            var Q0;
            Q0 = qSketchRegion(id + "F21", true);
            extrude(context, id + "F22", {"entities" : qUnion([Q0]), "operationType" : NewBodyOperationType.ADD, "endBound" : BoundingType.UP_TO_NEXT, "depth" : 25.4 * mm, "offsetDistance" : 25.4 * mm});
        }
    });
